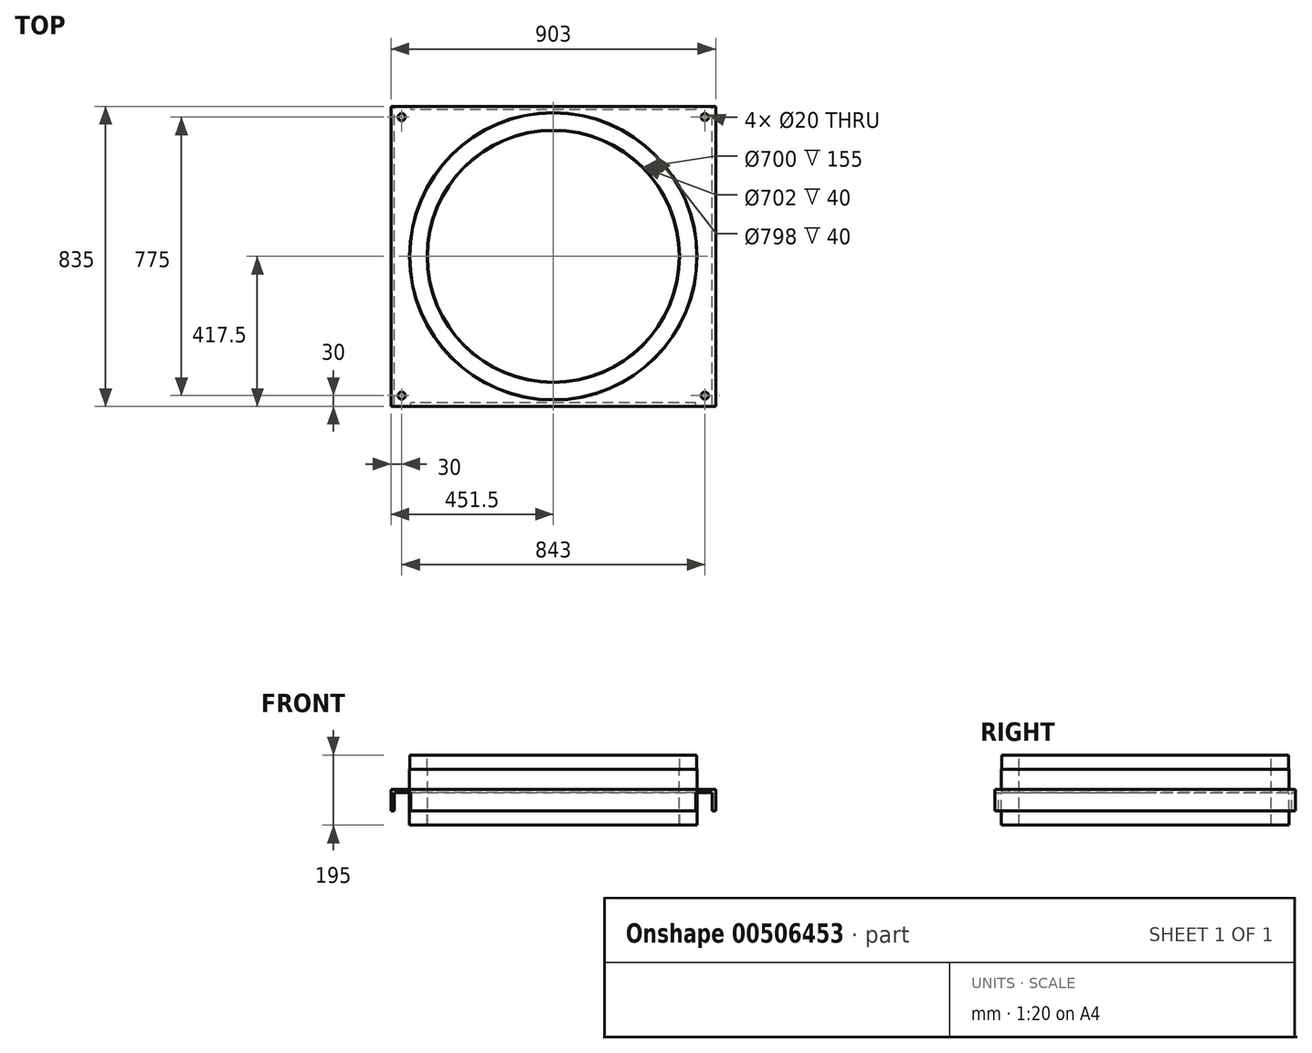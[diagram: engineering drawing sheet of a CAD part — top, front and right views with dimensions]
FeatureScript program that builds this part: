
annotation { "Feature Type Name" : "Feature", "Feature Type Description" : "" }
export const myFeature = defineFeature(function(context is Context, id is Id, definition is map)
    precondition{}
    {
        {
            var Q0;
            Q0=qCreatedBy(makeId("Front.planeOp"),FACE);
            var sketch = newSketch(context, id + "F0", { "sketchPlane" : qUnion([Q0])});
            skLineSegment(sketch, "E0", {"start": v(0, 74.87) * mm, "end": v(0, -73.71) * mm, "construction": true});
            skLineSegment(sketch, "E1", {"start": v(0, 374.84) * mm, "end": v(0, -528.94) * mm, "construction": true});
            skLineSegment(sketch, "E2", {"start": v(-350, -100) * mm, "end": v(-350, 55) * mm});
            skLineSegment(sketch, "E3", {"start": v(-350, 55) * mm, "end": v(-351, 55) * mm});
            skLineSegment(sketch, "E4", {"start": v(-351, 55) * mm, "end": v(-351, 95) * mm});
            skLineSegment(sketch, "E5", {"start": v(-351, 95) * mm, "end": v(-399, 95) * mm});
            skLineSegment(sketch, "E6", {"start": v(-399, 95) * mm, "end": v(-399, 55) * mm});
            skLineSegment(sketch, "E7", {"start": v(-399, 55) * mm, "end": v(-400, 55) * mm});
            skLineSegment(sketch, "E8", {"start": v(-400, 55) * mm, "end": v(-400, -100) * mm});
            skLineSegment(sketch, "E9", {"start": v(-400, -100) * mm, "end": v(-399, -100) * mm});
            skLineSegment(sketch, "E10", {"start": v(-399, -100) * mm, "end": v(-399, -60) * mm});
            skLineSegment(sketch, "E11", {"start": v(-399, -60) * mm, "end": v(-351, -60) * mm});
            skLineSegment(sketch, "E12", {"start": v(-351, -60) * mm, "end": v(-351, -100) * mm});
            skLineSegment(sketch, "E13", {"start": v(-351, -100) * mm, "end": v(-350, -100) * mm});
            skSolve(sketch);
        }
        {
            var Q0;
            Q0=qSketchRegion(id+"F0",true);
            var Q1;
            Q1=sQuery(id+"F0.wireOp",EDGE,"E1");
            revolve(context, id + "F1", {"entities" : qUnion([Q0]), "axis" : qUnion([Q1]), "revolveType" : RevolveType.FULL});
        }
        {
            var Q0;
            Q0=qCreatedBy(makeId("Top.planeOp"),FACE);
            var sketch = newSketch(context, id + "F2", { "sketchPlane" : qUnion([Q0])});
            skLineSegment(sketch, "E14.bottom", {"start": v(451.5, 417.5) * mm, "end": v(-451.5, 417.5) * mm});
            skLineSegment(sketch, "E14.top", {"start": v(451.5, -417.5) * mm, "end": v(-451.5, -417.5) * mm});
            skLineSegment(sketch, "E14.left", {"start": v(451.5, 417.5) * mm, "end": v(451.5, -417.5) * mm});
            skLineSegment(sketch, "E14.right", {"start": v(-451.5, 417.5) * mm, "end": v(-451.5, -417.5) * mm});
            skPoint(sketch, "E14.middle", {"position": v(0, 0) * mm});
            skCircle(sketch, "E15.0", {"center": v(0, 0) * mm, "radius": 351 * mm});
            skCircle(sketch, "E16.0", {"center": v(0, 0) * mm, "radius": 350 * mm});
            skCircle(sketch, "E17", {"center": v(0, 0) * mm, "radius": 400 * mm});
            skLineSegment(sketch, "E18", {"start": v(0, 0) * mm, "end": v(0, 773.78) * mm, "construction": true});
            skLineSegment(sketch, "E19", {"start": v(0, 0) * mm, "end": v(1007.48, 0) * mm, "construction": true});
            skCircle(sketch, "E20", {"center": v(421.5, 387.5) * mm, "radius": 10 * mm});
            skCircle(sketch, "E21.MirrorC", {"center": v(-421.5, 387.5) * mm, "radius": 10 * mm});
            skCircle(sketch, "E22.MirrorC", {"center": v(421.5, -387.5) * mm, "radius": 10 * mm});
            skCircle(sketch, "E23.MirrorC", {"center": v(-421.5, -387.5) * mm, "radius": 10 * mm});
            skSolve(sketch);
        }
        {
            var Q0;
            Q0=qSketchRegion(id+"F2",true);
            extrude(context, id + "F3", {"entities" : qUnion([Q0]), "operationType" : NewBodyOperationType.ADD, "oppositeDirection" : true, "depth" : 10 * mm});
        }
        {
            var Q0;
            Q0=makeQuery(id+"F3.opExtrude","CAP_FACE",FACE,{"disambiguationData":[OSD([sQuery(id+"F2.wireOp",EDGE,"E14.bottom"),sQuery(id+"F2.wireOp",EDGE,"E14.top"),sQuery(id+"F2.wireOp",EDGE,"E14.left"),sQuery(id+"F2.wireOp",EDGE,"E14.right"),sQuery(id+"F2.wireOp",EDGE,"E17"),sQuery(id+"F2.wireOp",EDGE,"E20"),sQuery(id+"F2.wireOp",EDGE,"E21.MirrorC"),sQuery(id+"F2.wireOp",EDGE,"E22.MirrorC"),sQuery(id+"F2.wireOp",EDGE,"E23.MirrorC")])],"isStart":false});
            var sketch = newSketch(context, id + "F4", { "sketchPlane" : qUnion([Q0])});
            skLineSegment(sketch, "E24", {"start": v(0, 0) * mm, "end": v(-1098.02, 0) * mm, "construction": true});
            skLineSegment(sketch, "E25", {"start": v(0, 0) * mm, "end": v(0, -1084.2) * mm, "construction": true});
            skLineSegment(sketch, "E26.bottom", {"start": v(396.5, 417.5) * mm, "end": v(-396.5, 417.5) * mm});
            skLineSegment(sketch, "E26.top", {"start": v(396.5, 407.5) * mm, "end": v(-396.5, 407.5) * mm});
            skLineSegment(sketch, "E26.left", {"start": v(396.5, 417.5) * mm, "end": v(396.5, 407.5) * mm});
            skLineSegment(sketch, "E26.right", {"start": v(-396.5, 417.5) * mm, "end": v(-396.5, 407.5) * mm});
            skLineSegment(sketch, "E27.bottom", {"start": v(-451.5, 417.5) * mm, "end": v(-441.5, 417.5) * mm});
            skLineSegment(sketch, "E27.top", {"start": v(-451.5, -417.5) * mm, "end": v(-441.5, -417.5) * mm});
            skLineSegment(sketch, "E27.left", {"start": v(-451.5, 417.5) * mm, "end": v(-451.5, -417.5) * mm});
            skLineSegment(sketch, "E27.right", {"start": v(-441.5, 417.5) * mm, "end": v(-441.5, -417.5) * mm});
            skLineSegment(sketch, "E28.MirrorCS", {"start": v(396.5, -417.5) * mm, "end": v(396.5, -407.5) * mm});
            skLineSegment(sketch, "E29.MirrorCS", {"start": v(-396.5, -417.5) * mm, "end": v(-396.5, -407.5) * mm});
            skLineSegment(sketch, "E30.MirrorCS", {"start": v(396.5, -407.5) * mm, "end": v(-396.5, -407.5) * mm});
            skLineSegment(sketch, "E31.MirrorCS", {"start": v(396.5, -417.5) * mm, "end": v(-396.5, -417.5) * mm});
            skLineSegment(sketch, "E32.MirrorCS", {"start": v(451.5, -417.5) * mm, "end": v(441.5, -417.5) * mm});
            skLineSegment(sketch, "E33.MirrorCS", {"start": v(451.5, 417.5) * mm, "end": v(441.5, 417.5) * mm});
            skLineSegment(sketch, "E34.MirrorCS", {"start": v(451.5, 417.5) * mm, "end": v(451.5, -417.5) * mm});
            skLineSegment(sketch, "E35.MirrorCS", {"start": v(441.5, 417.5) * mm, "end": v(441.5, -417.5) * mm});
            skLineSegment(sketch, "E36.MirrorCS", {"start": v(0, 0) * mm, "end": v(1098.02, 0) * mm, "construction": true});
            skSolve(sketch);
        }
        {
            var Q0;
            Q0=qSketchRegion(id+"F4",true);
            extrude(context, id + "F5", {"entities" : qUnion([Q0]), "operationType" : NewBodyOperationType.ADD, "depth" : 50 * mm});
        }
    });
